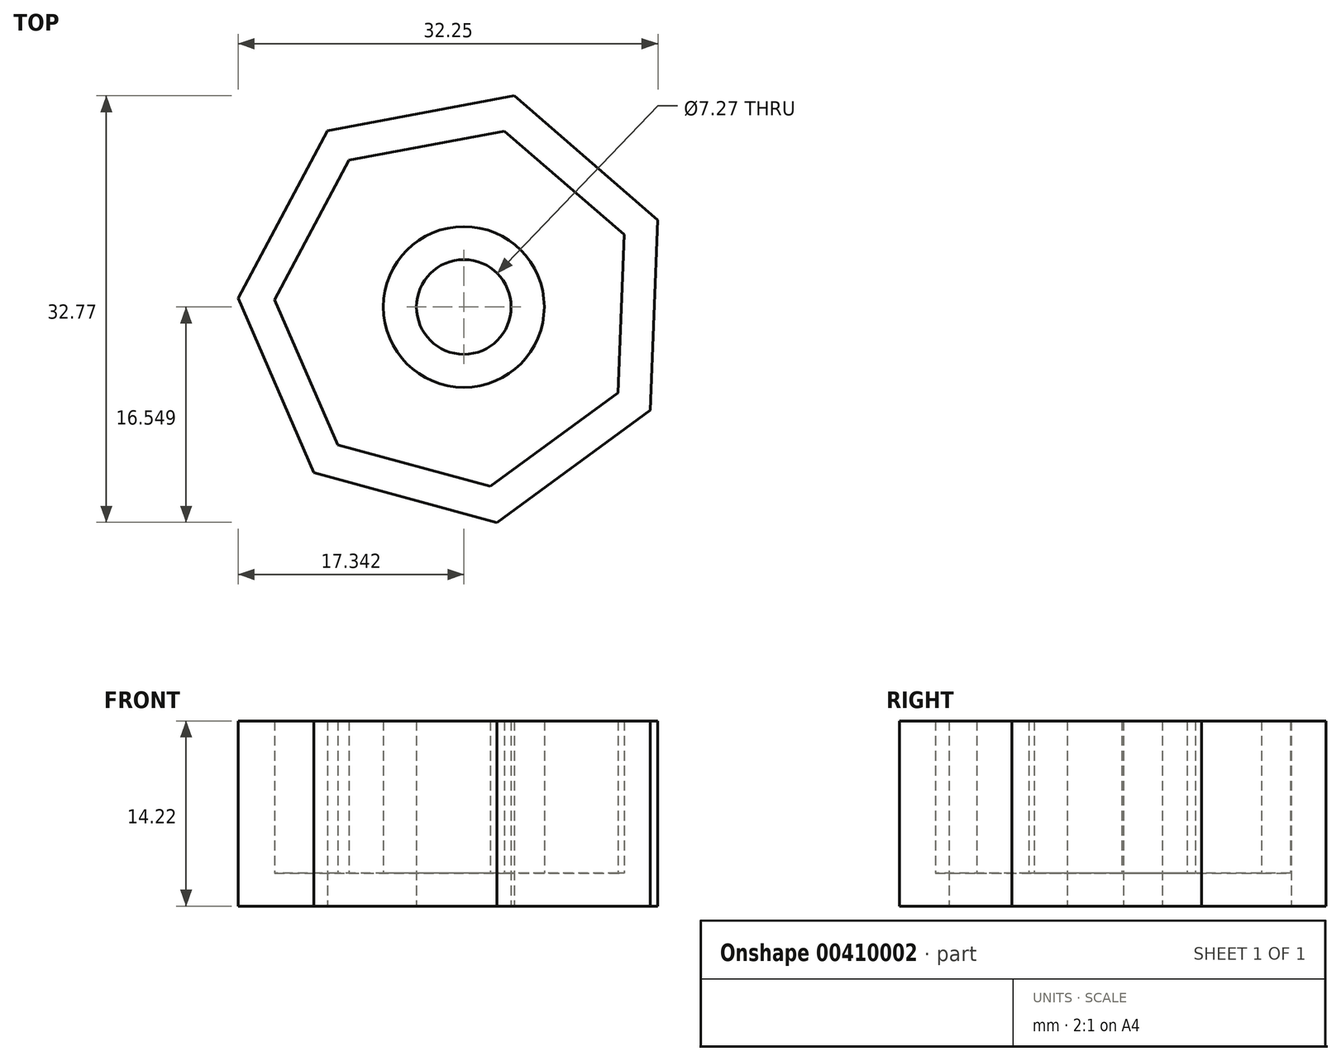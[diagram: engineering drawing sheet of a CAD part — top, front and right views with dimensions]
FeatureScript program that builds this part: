
annotation { "Feature Type Name" : "Feature", "Feature Type Description" : "" }
export const myFeature = defineFeature(function(context is Context, id is Id, definition is map)
    precondition{}
    {
        {
            var Q0;
            Q0=qCreatedBy(makeId("Top.planeOp"),FACE);
            var sketch = newSketch(context, id + "F0", { "sketchPlane" : qUnion([Q0])});
            skPoint(sketch, "E0.0.midPoint", {"position": v(-43.23, 27.3) * mm});
            skPoint(sketch, "E1.0.midPoint", {"position": v(10.34, 0) * mm});
            skLineSegment(sketch, "E2.0", {"start": v(-3.32, -10.6) * mm, "end": v(-17.4, -6.78) * mm});
            skLineSegment(sketch, "E2.1", {"start": v(-17.4, -6.78) * mm, "end": v(-23.21, 6.62) * mm});
            skLineSegment(sketch, "E2.2", {"start": v(-23.21, 6.62) * mm, "end": v(-16.35, 19.5) * mm});
            skLineSegment(sketch, "E2.3", {"start": v(-16.35, 19.5) * mm, "end": v(-2, 22.18) * mm});
            skLineSegment(sketch, "E2.4", {"start": v(-2, 22.18) * mm, "end": v(9.04, 12.63) * mm});
            skLineSegment(sketch, "E2.5", {"start": v(9.04, 12.63) * mm, "end": v(8.45, -1.96) * mm});
            skLineSegment(sketch, "E2.6", {"start": v(8.45, -1.96) * mm, "end": v(-3.32, -10.6) * mm});
            skPoint(sketch, "E2.0.midPoint", {"position": v(-10.36, -8.69) * mm});
            skPoint(sketch, "E3.orphan", {"position": v(-46.75, 27.3) * mm});
            skPoint(sketch, "E0.1.start.orphan", {"position": v(-39.7, 27.3) * mm});
            skPoint(sketch, "E0.cCircle.center.orphan", {"position": v(-43.23, 25.26) * mm});
            skPoint(sketch, "E1.1.start.orphan", {"position": v(-26.36, -92.78) * mm});
            skPoint(sketch, "E1.2.end.orphan", {"position": v(47.03, 92.78) * mm});
            skCircle(sketch, "E4", {"center": v(-5.87, 5.96) * mm, "radius": 3.64 * mm});
            skSolve(sketch);
        }
        {
            var Q0;
            Q0=makeQuery(id+"F0.imprint","IMPRINT",FACE,{"disambiguationData":[TD([[makeQuery(id+"F0.imprint","IMPRINT",EDGE,{"derivedFrom":sQuery(id+"F0.wireOp",EDGE,"E2.0")}),-1.0]])]});
            extrude(context, id + "F1", {"entities" : qUnion([Q0]), "depth" : 14.22 * mm});
        }
        {
            var Q0;
            Q0=makeQuery(id+"F1.opExtrude","CAP_FACE",FACE,{"disambiguationData":[OSD([sQuery(id+"F0.wireOp",EDGE,"E2.0"),sQuery(id+"F0.wireOp",EDGE,"E2.1"),sQuery(id+"F0.wireOp",EDGE,"E2.2"),sQuery(id+"F0.wireOp",EDGE,"E2.3"),sQuery(id+"F0.wireOp",EDGE,"E2.4"),sQuery(id+"F0.wireOp",EDGE,"E2.5"),sQuery(id+"F0.wireOp",EDGE,"E2.6"),sQuery(id+"F0.wireOp",EDGE,"E4")])],"isStart":false});
            shell(context, id + "F2", {"entities" : qUnion([Q0]), "thickness" : 2.54 * mm});
        }
    });
